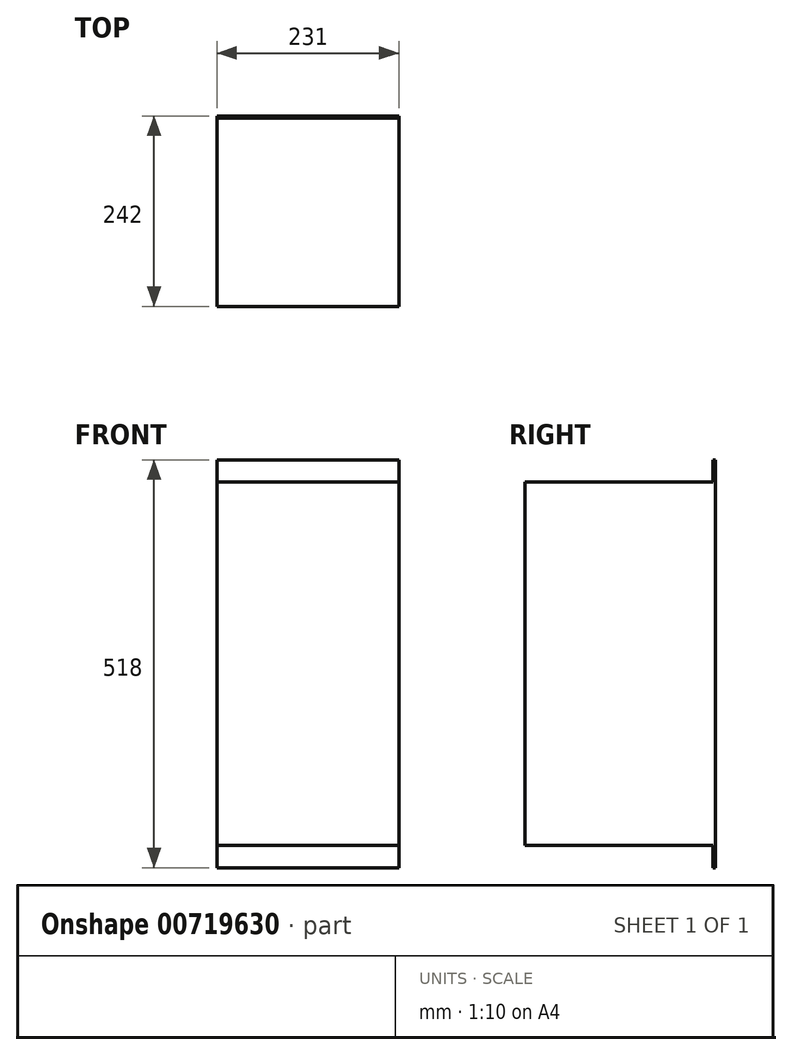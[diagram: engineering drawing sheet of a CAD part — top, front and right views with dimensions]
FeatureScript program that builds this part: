
annotation { "Feature Type Name" : "Feature", "Feature Type Description" : "" }
export const myFeature = defineFeature(function(context is Context, id is Id, definition is map)
    precondition{}
    {
        {
            var Q0;
            Q0=qCreatedBy(makeId("Front.planeOp"),FACE);
            var sketch = newSketch(context, id + "F0", { "sketchPlane" : qUnion([Q0])});
            skLineSegment(sketch, "E0.bottom", {"start": v(115.5, 259) * mm, "end": v(-115.5, 259) * mm});
            skLineSegment(sketch, "E0.top", {"start": v(115.5, -259) * mm, "end": v(-115.5, -259) * mm});
            skLineSegment(sketch, "E0.left", {"start": v(115.5, 259) * mm, "end": v(115.5, -259) * mm});
            skLineSegment(sketch, "E0.right", {"start": v(-115.5, 259) * mm, "end": v(-115.5, -259) * mm});
            skPoint(sketch, "E0.middle", {"position": v(0, 0) * mm});
            skLineSegment(sketch, "E1.bottom", {"start": v(115.5, 231) * mm, "end": v(-115.5, 231) * mm});
            skLineSegment(sketch, "E1.top", {"start": v(115.5, -231) * mm, "end": v(-115.5, -231) * mm});
            skLineSegment(sketch, "E1.left", {"start": v(115.5, 231) * mm, "end": v(115.5, -231) * mm});
            skLineSegment(sketch, "E1.right", {"start": v(-115.5, 231) * mm, "end": v(-115.5, -231) * mm});
            skSolve(sketch);
        }
        {
            var Q0;
            Q0=makeQuery(id+"F0.imprint","IMPRINT",FACE,{"disambiguationData":[TD([[makeQuery(id+"F0.imprint","IMPRINT",EDGE,{"derivedFrom":sQuery(id+"F0.wireOp",EDGE,"E1.bottom")}),1.0]])]});
            extrude(context, id + "F1", {"entities" : qUnion([Q0]), "depth" : 242 * mm, "offsetDistance" : 25 * mm});
        }
        {
            var Q0;
            {var subQ0=sQuery(id+"F0.wireOp",EDGE,"E0.bottom");Q0=makeQuery(id+"F0.imprint","IMPRINT",FACE,{"disambiguationData":[TD([[makeQuery(id+"F0.imprint","IMPRINT",EDGE,{"derivedFrom":subQ0}),1.0]])]});}
            var Q1;
            {var subQ0=sQuery(id+"F0.wireOp",EDGE,"E0.top");Q1=makeQuery(id+"F0.imprint","IMPRINT",FACE,{"disambiguationData":[TD([[makeQuery(id+"F0.imprint","IMPRINT",EDGE,{"derivedFrom":subQ0}),-1.0]])]});}
            extrude(context, id + "F2", {"entities" : qUnion([Q0, Q1]), "operationType" : NewBodyOperationType.ADD, "depth" : 3 * mm, "offsetDistance" : 25 * mm});
        }
    });
